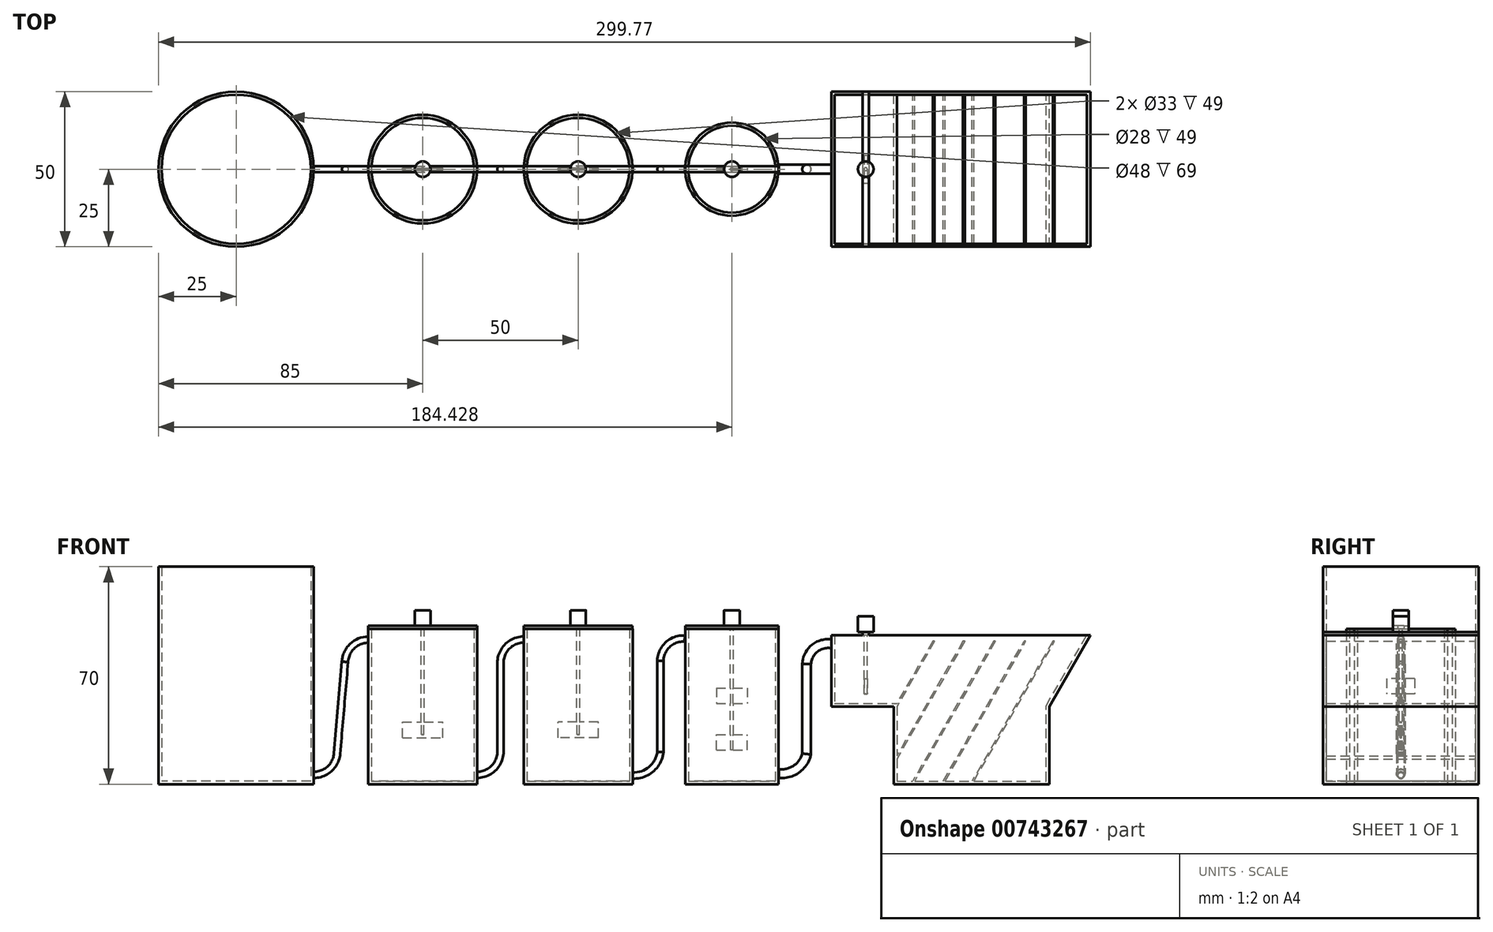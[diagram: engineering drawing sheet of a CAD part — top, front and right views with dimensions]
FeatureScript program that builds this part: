
annotation { "Feature Type Name" : "Feature", "Feature Type Description" : "" }
export const myFeature = defineFeature(function(context is Context, id is Id, definition is map)
    precondition{}
    {
        {
            var Q0;
            Q0=qCreatedBy(makeId("Top.planeOp"),FACE);
            var sketch = newSketch(context, id + "F0", { "sketchPlane" : qUnion([Q0])});
            skCircle(sketch, "E0", {"center": v(0, 0) * mm, "radius": 25 * mm});
            skCircle(sketch, "E1", {"center": v(159.43, 0) * mm, "radius": 15 * mm});
            skSolve(sketch);
        }
        {
            var Q0;
            Q0=makeQuery(id+"F0.imprint","IMPRINT",FACE,{"disambiguationData":[TD([[makeQuery(id+"F0.imprint","IMPRINT",EDGE,{"derivedFrom":sQuery(id+"F0.wireOp",EDGE,"E0")}),1.0]])]});
            extrude(context, id + "F1", {"entities" : qUnion([Q0]), "depth" : 70 * mm, "offsetDistance" : 25 * mm});
        }
        {
            var Q0;
            Q0=makeQuery(id+"F1.opExtrude","CAP_FACE",FACE,{"disambiguationData":[OSD([sQuery(id+"F0.wireOp",EDGE,"E0")])],"isStart":false});
            shell(context, id + "F2", {"entities" : qUnion([Q0]), "thickness" : 1 * mm});
        }
        {
            var Q0;
            Q0=qCreatedBy(makeId("Top.planeOp"),FACE);
            var sketch = newSketch(context, id + "F3", { "sketchPlane" : qUnion([Q0])});
            skCircle(sketch, "E2", {"center": v(60, 0) * mm, "radius": 17.5 * mm});
            skSolve(sketch);
        }
        {
            var Q0;
            Q0=makeQuery(id+"F3.imprint","IMPRINT",FACE,{"disambiguationData":[TD([[makeQuery(id+"F3.imprint","IMPRINT",EDGE,{"derivedFrom":sQuery(id+"F3.wireOp",EDGE,"E2")}),1.0]])]});
            extrude(context, id + "F4", {"entities" : qUnion([Q0]), "depth" : 50 * mm, "offsetDistance" : 25 * mm});
        }
        {
            var Q0;
            Q0=makeQuery(id+"F4.opExtrude","CAP_FACE",FACE,{"disambiguationData":[OSD([sQuery(id+"F3.wireOp",EDGE,"E2")])],"isStart":false});
            var Q1;
            Q1=makeQuery(id+"F4.opExtrude","CAP_FACE",FACE,{"disambiguationData":[OSD([sQuery(id+"F3.wireOp",EDGE,"7fbXtZi6-3e4z-6Rhc-ttlS-KZZd6jYo581z")])],"isStart":false});
            shell(context, id + "F5", {"entities" : qUnion([Q0, Q1]), "thickness" : 1 * mm});
        }
        {
            var Q0;
            Q0=makeQuery(id+"F4.opExtrude","CAP_FACE",FACE,{"disambiguationData":[OSD([sQuery(id+"F3.wireOp",EDGE,"E2")])],"isStart":false});
            var sketch = newSketch(context, id + "F6", { "sketchPlane" : qUnion([Q0])});
            skLineSegment(sketch, "E3.bottom", {"start": v(42.53, 1) * mm, "end": v(77.47, 1) * mm});
            skLineSegment(sketch, "E3.top", {"start": v(42.53, -1) * mm, "end": v(77.47, -1) * mm});
            skLineSegment(sketch, "E3.left", {"start": v(42.53, 1) * mm, "end": v(42.53, -1) * mm});
            skLineSegment(sketch, "E3.right", {"start": v(77.47, 1) * mm, "end": v(77.47, -1) * mm});
            skSolve(sketch);
        }
        {
            var Q0;
            {var subQ0=sQuery(id+"F6.wireOp",EDGE,"E3.left");Q0=makeQuery(id+"F6.imprint","IMPRINT",FACE,{"disambiguationData":[TD([[makeQuery(id+"F6.imprint","IMPRINT",EDGE,{"derivedFrom":subQ0}),1.0]])]});}
            var Q1;
            {var subQ0=sQuery(id+"F6.wireOp",EDGE,"E3.right");Q1=makeQuery(id+"F6.imprint","IMPRINT",FACE,{"disambiguationData":[TD([[makeQuery(id+"F6.imprint","IMPRINT",EDGE,{"derivedFrom":subQ0}),-1.0]])]});}
            var Q2;
            {var subQ0=sQuery(id+"F6.wireOp",EDGE,"E3.bottom");var subQ1=sQuery(id+"F3.wireOp",EDGE,"E2");var subQ2=makeQuery(id+"F5.opShell","OFFSET_EDGE",EDGE,{"disambiguationData":[OSD([subQ1]),TDD([makeQuery(id+"F4.opExtrude","CAP_EDGE",EDGE,{"disambiguationData":[OSD([subQ1])],"isStart":false})])]});var subQ3=makeQuery(id+"F6.imprint","INTERSECT",VERTEX,{"disambiguationData":[OD(0.0)],"derivedFrom":[subQ2,subQ0]});Q2=makeQuery(id+"F6.imprint","IMPRINT",FACE,{"disambiguationData":[TD([[makeQuery(id+"F6.imprint","IMPRINT",EDGE,{"disambiguationData":[TD([[subQ3,-1.0]])],"derivedFrom":subQ0}),-1.0]])]});}
            extrude(context, id + "F7", {"entities" : qUnion([Q0, Q1, Q2]), "operationType" : NewBodyOperationType.ADD, "depth" : 1 * mm, "offsetDistance" : 25 * mm});
        }
        {
            var Q0;
            Q0=makeQuery(id+"F7.opExtrude","CAP_FACE",FACE,{"disambiguationData":[OSD([sQuery(id+"F6.wireOp",EDGE,"E3.bottom"),sQuery(id+"F6.wireOp",EDGE,"E3.top"),sQuery(id+"F6.wireOp",EDGE,"E3.left"),sQuery(id+"F6.wireOp",EDGE,"E3.right")])],"isStart":false});
            var sketch = newSketch(context, id + "F8", { "sketchPlane" : qUnion([Q0])});
            skCircle(sketch, "E4.0.0", {"center": v(60, 0) * mm, "radius": 16.5 * mm});
            skCircle(sketch, "E5", {"center": v(60, 0) * mm, "radius": 2.5 * mm});
            skSolve(sketch);
        }
        {
            var Q0;
            {var subQ0=sQuery(id+"F8.wireOp",EDGE,"E5");var subQ1=makeQuery(id+"F7.opExtrude","CAP_EDGE",EDGE,{"disambiguationData":[OSD([sQuery(id+"F6.wireOp",EDGE,"E3.bottom")])],"isStart":false});var subQ2=makeQuery(id+"F8.imprint","INTERSECT",VERTEX,{"disambiguationData":[OD(0.0)],"derivedFrom":[subQ1,subQ0]});Q0=makeQuery(id+"F8.imprint","IMPRINT",FACE,{"disambiguationData":[TD([[makeQuery(id+"F8.imprint","IMPRINT",EDGE,{"disambiguationData":[TD([[subQ2,-1.0]])],"derivedFrom":subQ0}),1.0]])]});}
            var Q1;
            {var subQ0=sQuery(id+"F8.wireOp",EDGE,"E5");var subQ1=makeQuery(id+"F7.opExtrude","CAP_EDGE",EDGE,{"disambiguationData":[OSD([sQuery(id+"F6.wireOp",EDGE,"E3.top")])],"isStart":false});var subQ2=makeQuery(id+"F8.imprint","INTERSECT",VERTEX,{"disambiguationData":[OD(0.0)],"derivedFrom":[subQ1,subQ0]});Q1=makeQuery(id+"F8.imprint","IMPRINT",FACE,{"disambiguationData":[TD([[makeQuery(id+"F8.imprint","IMPRINT",EDGE,{"disambiguationData":[TD([[subQ2,-1.0]])],"derivedFrom":subQ0}),1.0]])]});}
            var Q2;
            {var subQ0=sQuery(id+"F8.wireOp",EDGE,"E5");var subQ1=makeQuery(id+"F7.opExtrude","CAP_EDGE",EDGE,{"disambiguationData":[OSD([sQuery(id+"F6.wireOp",EDGE,"E3.bottom")])],"isStart":false});var subQ2=makeQuery(id+"F8.imprint","INTERSECT",VERTEX,{"disambiguationData":[OD(0.0)],"derivedFrom":[subQ1,subQ0]});Q2=makeQuery(id+"F8.imprint","IMPRINT",FACE,{"disambiguationData":[TD([[makeQuery(id+"F8.imprint","IMPRINT",EDGE,{"disambiguationData":[TD([[subQ2,1.0]])],"derivedFrom":subQ0}),1.0]])]});}
            extrude(context, id + "F9", {"entities" : qUnion([Q0, Q1, Q2]), "operationType" : NewBodyOperationType.ADD, "depth" : 5 * mm, "offsetDistance" : 25 * mm});
        }
        {
            var Q0;
            Q0=makeQuery(id+"F9.opExtrude","CAP_FACE",FACE,{"disambiguationData":[OSD([sQuery(id+"F8.wireOp",EDGE,"E5")])],"isStart":false});
            var sketch = newSketch(context, id + "F10", { "sketchPlane" : qUnion([Q0])});
            skCircle(sketch, "E6", {"center": v(60, 0) * mm, "radius": 0.5 * mm});
            skSolve(sketch);
        }
        {
            var Q0;
            Q0=makeQuery(id+"F10.imprint","IMPRINT",FACE,{"disambiguationData":[TD([[makeQuery(id+"F10.imprint","IMPRINT",EDGE,{"derivedFrom":sQuery(id+"F10.wireOp",EDGE,"E6")}),1.0]])]});
            extrude(context, id + "F11", {"entities" : qUnion([Q0]), "operationType" : NewBodyOperationType.ADD, "oppositeDirection" : true, "depth" : 40 * mm, "offsetDistance" : 25 * mm});
        }
        {
            var Q0;
            Q0=qCreatedBy(makeId("Right.planeOp"),FACE);
            cPlane(context, id + "F12", {"entities" : qUnion([Q0]), "cplaneType" : CPlaneType.OFFSET, "offset" : 85 * mm, "width" : 150 * mm, "height" : 150 * mm});
        }
        {
            var Q0;
            Q0=makeQuery(id+"F4.opExtrude","CAP_FACE",FACE,{"disambiguationData":[OSD([sQuery(id+"F3.wireOp",EDGE,"E2")])],"isStart":true});
            cPlane(context, id + "F13", {"entities" : qUnion([Q0]), "cplaneType" : CPlaneType.OFFSET, "offset" : 20 * mm, "oppositeDirection" : true, "width" : 150 * mm, "height" : 150 * mm});
        }
        {
            var Q0;
            Q0=qCreatedBy(id+"F13.planeOp",FACE);
            var sketch = newSketch(context, id + "F14", { "sketchPlane" : qUnion([Q0])});
            skLineSegment(sketch, "E7.bottom", {"start": v(53.5, 0.3) * mm, "end": v(66.5, 0.3) * mm});
            skLineSegment(sketch, "E7.top", {"start": v(53.5, -0.3) * mm, "end": v(66.5, -0.3) * mm});
            skLineSegment(sketch, "E7.left", {"start": v(53.5, 0.3) * mm, "end": v(53.5, -0.3) * mm});
            skLineSegment(sketch, "E7.right", {"start": v(66.5, 0.3) * mm, "end": v(66.5, -0.3) * mm});
            skSolve(sketch);
        }
        {
            var Q0;
            Q0=makeQuery(id+"F14.imprint","IMPRINT",FACE,{"disambiguationData":[TD([[makeQuery(id+"F14.imprint","IMPRINT",EDGE,{"derivedFrom":sQuery(id+"F14.wireOp",EDGE,"E7.bottom")}),-1.0]])]});
            extrude(context, id + "F15", {"entities" : qUnion([Q0]), "operationType" : NewBodyOperationType.ADD, "depth" : 5 * mm, "offsetDistance" : 25 * mm});
        }
        {
            var Q0;
            Q0=makeQuery(id+"F4.opExtrude","SWEPT_BODY",BODY,{"disambiguationData":[OSD([sQuery(id+"F3.wireOp",EDGE,"E2")])]});
            var Q1;
            Q1=qCreatedBy(id+"F12.planeOp",FACE);
            mirror(context, id + "F16", {"entities" : qUnion([Q0]), "mirrorPlane" : qUnion([Q1])});
        }
        {
            var Q0;
            Q0=makeQuery(id+"F0.imprint","IMPRINT",FACE,{"disambiguationData":[TD([[makeQuery(id+"F0.imprint","IMPRINT",EDGE,{"derivedFrom":sQuery(id+"F0.wireOp",EDGE,"E1")}),1.0]])]});
            extrude(context, id + "F17", {"entities" : qUnion([Q0]), "depth" : 50 * mm, "offsetDistance" : 25 * mm});
        }
        {
            var Q0;
            Q0=makeQuery(id+"F17.opExtrude","CAP_FACE",FACE,{"disambiguationData":[OSD([sQuery(id+"F0.wireOp",EDGE,"E1")])],"isStart":false});
            shell(context, id + "F18", {"entities" : qUnion([Q0]), "thickness" : 1 * mm});
        }
        {
            var Q0;
            Q0=makeQuery(id+"F17.opExtrude","CAP_FACE",FACE,{"disambiguationData":[OSD([sQuery(id+"F0.wireOp",EDGE,"E1")])],"isStart":false});
            var sketch = newSketch(context, id + "F19", { "sketchPlane" : qUnion([Q0])});
            skLineSegment(sketch, "E8.bottom", {"start": v(144.46, 1) * mm, "end": v(174.4, 1) * mm});
            skLineSegment(sketch, "E8.top", {"start": v(144.46, -1) * mm, "end": v(174.4, -1) * mm});
            skLineSegment(sketch, "E8.left", {"start": v(144.46, 1) * mm, "end": v(144.46, -1) * mm});
            skLineSegment(sketch, "E8.right", {"start": v(174.4, 1) * mm, "end": v(174.4, -1) * mm});
            skSolve(sketch);
        }
        {
            var Q0;
            {var subQ0=sQuery(id+"F19.wireOp",EDGE,"E8.bottom");var subQ1=sQuery(id+"F0.wireOp",EDGE,"E1");var subQ2=makeQuery(id+"F18.opShell","OFFSET_EDGE",EDGE,{"disambiguationData":[OSD([subQ1]),TDD([makeQuery(id+"F17.opExtrude","CAP_EDGE",EDGE,{"disambiguationData":[OSD([subQ1])],"isStart":false})])]});var subQ3=makeQuery(id+"F19.imprint","INTERSECT",VERTEX,{"disambiguationData":[OD(0.0)],"derivedFrom":[subQ2,subQ0]});Q0=makeQuery(id+"F19.imprint","IMPRINT",FACE,{"disambiguationData":[TD([[makeQuery(id+"F19.imprint","IMPRINT",EDGE,{"disambiguationData":[TD([[subQ3,-1.0]])],"derivedFrom":subQ0}),-1.0]])]});}
            var Q1;
            {var subQ0=sQuery(id+"F19.wireOp",EDGE,"E8.left");Q1=makeQuery(id+"F19.imprint","IMPRINT",FACE,{"disambiguationData":[TD([[makeQuery(id+"F19.imprint","IMPRINT",EDGE,{"derivedFrom":subQ0}),1.0]])]});}
            var Q2;
            {var subQ0=sQuery(id+"F19.wireOp",EDGE,"E8.right");Q2=makeQuery(id+"F19.imprint","IMPRINT",FACE,{"disambiguationData":[TD([[makeQuery(id+"F19.imprint","IMPRINT",EDGE,{"derivedFrom":subQ0}),-1.0]])]});}
            extrude(context, id + "F20", {"entities" : qUnion([Q0, Q1, Q2]), "operationType" : NewBodyOperationType.ADD, "depth" : 1 * mm, "offsetDistance" : 25 * mm});
        }
        {
            var Q0;
            Q0=makeQuery(id+"F20.opExtrude","CAP_FACE",FACE,{"disambiguationData":[OSD([sQuery(id+"F19.wireOp",EDGE,"E8.bottom"),sQuery(id+"F19.wireOp",EDGE,"E8.top"),sQuery(id+"F19.wireOp",EDGE,"E8.left"),sQuery(id+"F19.wireOp",EDGE,"E8.right")])],"isStart":false});
            var sketch = newSketch(context, id + "F21", { "sketchPlane" : qUnion([Q0])});
            skArc(sketch, "E9.0", {"start": v(173.4, 1) * mm, "mid": v(159.43, 14) * mm, "end": v(145.46, 1) * mm});
            skCircle(sketch, "E10", {"center": v(159.43, 0) * mm, "radius": 0.5 * mm});
            skSolve(sketch);
        }
        {
            var Q0;
            Q0=makeQuery(id+"F21.imprint","IMPRINT",FACE,{"disambiguationData":[TD([[makeQuery(id+"F21.imprint","IMPRINT",EDGE,{"derivedFrom":sQuery(id+"F21.wireOp",EDGE,"E10")}),1.0]])]});
            extrude(context, id + "F22", {"entities" : qUnion([Q0]), "operationType" : NewBodyOperationType.ADD, "oppositeDirection" : true, "depth" : 40 * mm, "offsetDistance" : 25 * mm});
        }
        {
            var Q0;
            Q0=makeQuery(id+"F20.opExtrude","CAP_FACE",FACE,{"disambiguationData":[OSD([sQuery(id+"F19.wireOp",EDGE,"E8.bottom"),sQuery(id+"F19.wireOp",EDGE,"E8.top"),sQuery(id+"F19.wireOp",EDGE,"E8.left"),sQuery(id+"F19.wireOp",EDGE,"E8.right")])],"isStart":false});
            cPlane(context, id + "F23", {"entities" : qUnion([Q0]), "cplaneType" : CPlaneType.OFFSET, "offset" : 35 * mm, "oppositeDirection" : true, "width" : 150 * mm, "height" : 150 * mm});
        }
        {
            var Q0;
            Q0=qCreatedBy(id+"F23.planeOp",FACE);
            var sketch = newSketch(context, id + "F24", { "sketchPlane" : qUnion([Q0])});
            skLineSegment(sketch, "E11.bottom", {"start": v(154.43, 0.3) * mm, "end": v(164.43, 0.3) * mm});
            skLineSegment(sketch, "E11.top", {"start": v(154.43, -0.3) * mm, "end": v(164.43, -0.3) * mm});
            skLineSegment(sketch, "E11.left", {"start": v(154.43, 0.3) * mm, "end": v(154.43, -0.3) * mm});
            skLineSegment(sketch, "E11.right", {"start": v(164.43, 0.3) * mm, "end": v(164.43, -0.3) * mm});
            skSolve(sketch);
        }
        {
            var Q0;
            Q0=makeQuery(id+"F24.imprint","IMPRINT",FACE,{"disambiguationData":[TD([[makeQuery(id+"F24.imprint","IMPRINT",EDGE,{"derivedFrom":sQuery(id+"F24.wireOp",EDGE,"E11.bottom")}),-1.0]])]});
            extrude(context, id + "F25", {"entities" : qUnion([Q0]), "operationType" : NewBodyOperationType.ADD, "oppositeDirection" : true, "depth" : 5 * mm, "offsetDistance" : 25 * mm});
        }
        {
            var Q0;
            Q0=makeQuery(id+"F20.opExtrude","CAP_FACE",FACE,{"disambiguationData":[OSD([sQuery(id+"F19.wireOp",EDGE,"E8.bottom"),sQuery(id+"F19.wireOp",EDGE,"E8.top"),sQuery(id+"F19.wireOp",EDGE,"E8.left"),sQuery(id+"F19.wireOp",EDGE,"E8.right")])],"isStart":false});
            cPlane(context, id + "F26", {"entities" : qUnion([Q0]), "cplaneType" : CPlaneType.OFFSET, "offset" : 25 * mm, "oppositeDirection" : true, "width" : 150 * mm, "height" : 150 * mm});
        }
        {
            var Q0;
            Q0=qCreatedBy(id+"F26.planeOp",FACE);
            var sketch = newSketch(context, id + "F27", { "sketchPlane" : qUnion([Q0])});
            skLineSegment(sketch, "E12.0", {"start": v(154.43, 0.3) * mm, "end": v(159.03, 0.3) * mm});
            skPoint(sketch, "E13.0", {"position": v(154.43, 0) * mm});
            skLineSegment(sketch, "E14.0", {"start": v(154.43, 0.3) * mm, "end": v(154.43, -0.3) * mm});
            skLineSegment(sketch, "E15.0", {"start": v(154.43, -0.3) * mm, "end": v(159.03, -0.3) * mm});
            skLineSegment(sketch, "E16.0", {"start": v(159.83, 0.3) * mm, "end": v(164.43, 0.3) * mm});
            skLineSegment(sketch, "E17.0", {"start": v(164.43, 0.3) * mm, "end": v(164.43, -0.3) * mm});
            skLineSegment(sketch, "E18.0", {"start": v(159.83, -0.3) * mm, "end": v(164.43, -0.3) * mm});
            skLineSegment(sketch, "E19", {"start": v(159.03, 0.3) * mm, "end": v(159.83, 0.3) * mm});
            skLineSegment(sketch, "E20", {"start": v(159.83, -0.3) * mm, "end": v(159.03, -0.3) * mm});
            skSolve(sketch);
        }
        {
            var Q0;
            Q0=makeQuery(id+"F27.imprint","IMPRINT",FACE,{"disambiguationData":[TD([[makeQuery(id+"F27.imprint","IMPRINT",EDGE,{"derivedFrom":sQuery(id+"F27.wireOp",EDGE,"E12.0")}),-1.0]])]});
            extrude(context, id + "F28", {"entities" : qUnion([Q0]), "operationType" : NewBodyOperationType.ADD, "depth" : 5 * mm, "offsetDistance" : 25 * mm});
        }
        {
            var Q0;
            Q0=makeQuery(id+"F20.opExtrude","CAP_FACE",FACE,{"disambiguationData":[OSD([sQuery(id+"F19.wireOp",EDGE,"E8.bottom"),sQuery(id+"F19.wireOp",EDGE,"E8.top"),sQuery(id+"F19.wireOp",EDGE,"E8.left"),sQuery(id+"F19.wireOp",EDGE,"E8.right")])],"isStart":false});
            var sketch = newSketch(context, id + "F29", { "sketchPlane" : qUnion([Q0])});
            skCircle(sketch, "E21", {"center": v(159.43, 0) * mm, "radius": 2.5 * mm});
            skPoint(sketch, "E21.centerSnap0", {"position": v(159.43, -1) * mm});
            skSolve(sketch);
        }
        {
            var Q0;
            {var subQ0=sQuery(id+"F29.wireOp",EDGE,"E21");var subQ1=makeQuery(id+"F20.opExtrude","CAP_EDGE",EDGE,{"disambiguationData":[OSD([sQuery(id+"F19.wireOp",EDGE,"E8.bottom")])],"isStart":false});var subQ2=makeQuery(id+"F29.imprint","INTERSECT",VERTEX,{"disambiguationData":[OD(0.0)],"derivedFrom":[subQ1,subQ0]});Q0=makeQuery(id+"F29.imprint","IMPRINT",FACE,{"disambiguationData":[TD([[makeQuery(id+"F29.imprint","IMPRINT",EDGE,{"disambiguationData":[TD([[subQ2,1.0]])],"derivedFrom":subQ0}),1.0]])]});}
            var Q1;
            {var subQ0=sQuery(id+"F29.wireOp",EDGE,"E21");var subQ1=makeQuery(id+"F20.opExtrude","CAP_EDGE",EDGE,{"disambiguationData":[OSD([sQuery(id+"F19.wireOp",EDGE,"E8.top")])],"isStart":false});var subQ2=makeQuery(id+"F29.imprint","INTERSECT",VERTEX,{"disambiguationData":[OD(0.0)],"derivedFrom":[subQ1,subQ0]});Q1=makeQuery(id+"F29.imprint","IMPRINT",FACE,{"disambiguationData":[TD([[makeQuery(id+"F29.imprint","IMPRINT",EDGE,{"disambiguationData":[TD([[subQ2,-1.0]])],"derivedFrom":subQ0}),1.0]])]});}
            var Q2;
            {var subQ0=sQuery(id+"F29.wireOp",EDGE,"E21");var subQ1=makeQuery(id+"F20.opExtrude","CAP_EDGE",EDGE,{"disambiguationData":[OSD([sQuery(id+"F19.wireOp",EDGE,"E8.bottom")])],"isStart":false});var subQ2=makeQuery(id+"F29.imprint","INTERSECT",VERTEX,{"disambiguationData":[OD(0.0)],"derivedFrom":[subQ1,subQ0]});Q2=makeQuery(id+"F29.imprint","IMPRINT",FACE,{"disambiguationData":[TD([[makeQuery(id+"F29.imprint","IMPRINT",EDGE,{"disambiguationData":[TD([[subQ2,-1.0]])],"derivedFrom":subQ0}),1.0]])]});}
            extrude(context, id + "F30", {"entities" : qUnion([Q0, Q1, Q2]), "operationType" : NewBodyOperationType.ADD, "depth" : 5 * mm, "offsetDistance" : 25 * mm});
        }
        {
            var Q0;
            Q0=qCreatedBy(makeId("Front.planeOp"),FACE);
            var sketch = newSketch(context, id + "F31", { "sketchPlane" : qUnion([Q0])});
            skLineSegment(sketch, "E22", {"start": v(191.49, 48) * mm, "end": v(191.49, 25) * mm});
            skLineSegment(sketch, "E23", {"start": v(191.49, 25) * mm, "end": v(211.49, 25) * mm});
            skLineSegment(sketch, "E24", {"start": v(211.49, 25) * mm, "end": v(211.49, 0) * mm});
            skLineSegment(sketch, "E25", {"start": v(211.49, 0) * mm, "end": v(261.49, 0) * mm});
            skLineSegment(sketch, "E26", {"start": v(261.49, 0) * mm, "end": v(261.49, 25) * mm});
            skLineSegment(sketch, "E27", {"start": v(261.49, 25) * mm, "end": v(274.77, 48) * mm});
            skLineSegment(sketch, "E28", {"start": v(274.77, 48) * mm, "end": v(191.49, 48) * mm});
            skSolve(sketch);
        }
        {
            var Q0;
            Q0=makeQuery(id+"F31.imprint","IMPRINT",FACE,{"disambiguationData":[TD([[makeQuery(id+"F31.imprint","IMPRINT",EDGE,{"derivedFrom":sQuery(id+"F31.wireOp",EDGE,"E22")}),1.0]])]});
            extrude(context, id + "F32", {"entities" : qUnion([Q0]), "endBound" : BoundingType.SYMMETRIC, "depth" : 50 * mm, "offsetDistance" : 25 * mm});
        }
        {
            var Q0;
            Q0=makeQuery(id+"F32.opExtrude","SWEPT_FACE",FACE,{"disambiguationData":[OSD([sQuery(id+"F31.wireOp",EDGE,"E28")])]});
            shell(context, id + "F33", {"entities" : qUnion([Q0]), "thickness" : 1 * mm});
        }
        {
            var Q0;
            Q0=qCreatedBy(makeId("Front.planeOp"),FACE);
            var sketch = newSketch(context, id + "F34", { "sketchPlane" : qUnion([Q0])});
            skLineSegment(sketch, "E29.0", {"start": v(264.37, 48) * mm, "end": v(263.8, 48) * mm});
            skLineSegment(sketch, "E30.0", {"start": v(212.49, 26) * mm, "end": v(212.49, 25) * mm});
            skLineSegment(sketch, "E31.0", {"start": v(227.42, 1) * mm, "end": v(228, 1) * mm});
            skLineSegment(sketch, "E32", {"start": v(212.49, 26) * mm, "end": v(224.03, 46) * mm});
            skLineSegment(sketch, "E33", {"start": v(212.49, 25) * mm, "end": v(224.61, 46) * mm});
            skLineSegment(sketch, "E34", {"start": v(263.22, 46) * mm, "end": v(237.24, 1) * mm});
            skLineSegment(sketch, "E35", {"start": v(253.98, 46) * mm, "end": v(228, 1) * mm});
            skLineSegment(sketch, "E36", {"start": v(253.4, 46) * mm, "end": v(227.42, 1) * mm});
            skLineSegment(sketch, "E37", {"start": v(236.66, 1) * mm, "end": v(262.64, 46) * mm});
            skPoint(sketch, "E38.0.2.start.orphan", {"position": v(191.49, 48) * mm});
            skPoint(sketch, "E38.0.3.start.orphan", {"position": v(191.49, 25) * mm});
            skPoint(sketch, "E38.0.4.start.orphan", {"position": v(211.49, 25) * mm});
            skLineSegment(sketch, "E39.trimOffspring", {"start": v(236.66, 1) * mm, "end": v(237.24, 1) * mm});
            skPoint(sketch, "E38.0.5.start.orphan", {"position": v(211.49, 0) * mm});
            skPoint(sketch, "E40.orphan", {"position": v(212.49, 1) * mm});
            skPoint(sketch, "E41.orphan", {"position": v(260.49, 1) * mm});
            skPoint(sketch, "E38.0.6.start.orphan", {"position": v(261.49, 0) * mm});
            skLineSegment(sketch, "E42.trimOffspring", {"start": v(225.77, 48) * mm, "end": v(225.19, 48) * mm});
            skLineSegment(sketch, "E43.trimOffspring", {"start": v(255.14, 48) * mm, "end": v(254.56, 48) * mm});
            skPoint(sketch, "E38.0.0.end.orphan", {"position": v(274.77, 48) * mm});
            skPoint(sketch, "E38.0.0.start.orphan", {"position": v(261.49, 25) * mm});
            skLineSegment(sketch, "E44.0.0", {"start": v(261.49, 25) * mm, "end": v(274.77, 48) * mm});
            skLineSegment(sketch, "E44.0.1", {"start": v(274.77, 48) * mm, "end": v(191.49, 48) * mm});
            skLineSegment(sketch, "E44.0.2", {"start": v(191.49, 48) * mm, "end": v(191.49, 25) * mm});
            skLineSegment(sketch, "E44.0.3", {"start": v(191.49, 25) * mm, "end": v(211.49, 25) * mm});
            skLineSegment(sketch, "E44.0.4", {"start": v(211.49, 25) * mm, "end": v(211.49, 0) * mm});
            skLineSegment(sketch, "E44.0.5", {"start": v(211.49, 0) * mm, "end": v(261.49, 0) * mm});
            skLineSegment(sketch, "E44.0.6", {"start": v(261.49, 0) * mm, "end": v(261.49, 25) * mm});
            skLineSegment(sketch, "E45.0", {"start": v(212.49, 1) * mm, "end": v(260.49, 1) * mm});
            skLineSegment(sketch, "E46.0", {"start": v(212.49, 26) * mm, "end": v(212.49, 1) * mm});
            skLineSegment(sketch, "E47", {"start": v(218.19, 1) * mm, "end": v(244.17, 46) * mm});
            skLineSegment(sketch, "E48", {"start": v(217.6, 1) * mm, "end": v(243.59, 46) * mm});
            skLineSegment(sketch, "E49", {"start": v(212.49, 8.13) * mm, "end": v(234.35, 46) * mm});
            skLineSegment(sketch, "E50", {"start": v(212.49, 9.13) * mm, "end": v(233.77, 46) * mm});
            skLineSegment(sketch, "E51", {"start": v(224.03, 46) * mm, "end": v(224.61, 46) * mm});
            skLineSegment(sketch, "E52.trimOffspring", {"start": v(262.64, 46) * mm, "end": v(263.22, 46) * mm});
            skLineSegment(sketch, "E53.trimOffspring", {"start": v(253.4, 46) * mm, "end": v(253.98, 46) * mm});
            skLineSegment(sketch, "E54.trimOffspring", {"start": v(243.59, 46) * mm, "end": v(244.17, 46) * mm});
            skLineSegment(sketch, "E55.trimOffspring", {"start": v(233.77, 46) * mm, "end": v(234.35, 46) * mm});
            skSolve(sketch);
        }
        {
            var Q0;
            {var subQ0=sQuery(id+"F34.wireOp",EDGE,"E32");Q0=makeQuery(id+"F34.imprint","IMPRINT",FACE,{"disambiguationData":[TD([[makeQuery(id+"F34.imprint","IMPRINT",EDGE,{"derivedFrom":subQ0}),-1.0]])]});}
            var Q1;
            {var subQ0=sQuery(id+"F34.wireOp",EDGE,"E49");Q1=makeQuery(id+"F34.imprint","IMPRINT",FACE,{"disambiguationData":[TD([[makeQuery(id+"F34.imprint","IMPRINT",EDGE,{"derivedFrom":subQ0}),1.0]])]});}
            var Q2;
            {var subQ0=sQuery(id+"F34.wireOp",EDGE,"E47");Q2=makeQuery(id+"F34.imprint","IMPRINT",FACE,{"disambiguationData":[TD([[makeQuery(id+"F34.imprint","IMPRINT",EDGE,{"derivedFrom":subQ0}),1.0]])]});}
            var Q3;
            {var subQ0=sQuery(id+"F34.wireOp",EDGE,"E35");Q3=makeQuery(id+"F34.imprint","IMPRINT",FACE,{"disambiguationData":[TD([[makeQuery(id+"F34.imprint","IMPRINT",EDGE,{"derivedFrom":subQ0}),-1.0]])]});}
            var Q4;
            {var subQ0=sQuery(id+"F34.wireOp",EDGE,"E34");Q4=makeQuery(id+"F34.imprint","IMPRINT",FACE,{"disambiguationData":[TD([[makeQuery(id+"F34.imprint","IMPRINT",EDGE,{"derivedFrom":subQ0}),-1.0]])]});}
            extrude(context, id + "F35", {"entities" : qUnion([Q0, Q1, Q2, Q3, Q4]), "operationType" : NewBodyOperationType.ADD, "endBound" : BoundingType.SYMMETRIC, "depth" : 50 * mm, "offsetDistance" : 25 * mm});
        }
        {
            var Q0;
            Q0=makeQuery(id+"F32.opExtrude","SWEPT_FACE",FACE,{"disambiguationData":[OSD([sQuery(id+"F31.wireOp",EDGE,"E28")])]});
            var sketch = newSketch(context, id + "F36", { "sketchPlane" : qUnion([Q0])});
            skLineSegment(sketch, "E56.bottom", {"start": v(201.49, 25) * mm, "end": v(203.49, 25) * mm});
            skLineSegment(sketch, "E56.top", {"start": v(201.49, -25) * mm, "end": v(203.49, -25) * mm});
            skLineSegment(sketch, "E56.left", {"start": v(201.49, 25) * mm, "end": v(201.49, -25) * mm});
            skLineSegment(sketch, "E56.right", {"start": v(203.49, 25) * mm, "end": v(203.49, -25) * mm});
            skSolve(sketch);
        }
        {
            var Q0;
            {var subQ0=sQuery(id+"F36.wireOp",EDGE,"E56.left");var subQ1=sQuery(id+"F31.wireOp",EDGE,"E28");var subQ2=makeQuery(id+"F33.opShell","OFFSET_EDGE",EDGE,{"disambiguationData":[OSD([subQ1]),TDD([makeQuery(id+"F32.opExtrude","CAP_EDGE",EDGE,{"disambiguationData":[OSD([subQ1])],"isStart":true})])]});var subQ3=makeQuery(id+"F36.imprint","INTERSECT",VERTEX,{"derivedFrom":[subQ2,subQ0]});Q0=makeQuery(id+"F36.imprint","IMPRINT",FACE,{"disambiguationData":[TD([[makeQuery(id+"F36.imprint","IMPRINT",EDGE,{"disambiguationData":[TD([[subQ3,-1.0]])],"derivedFrom":subQ0}),1.0]])]});}
            var Q1;
            {var subQ0=sQuery(id+"F36.wireOp",EDGE,"E56.top");Q1=makeQuery(id+"F36.imprint","IMPRINT",FACE,{"disambiguationData":[TD([[makeQuery(id+"F36.imprint","IMPRINT",EDGE,{"derivedFrom":subQ0}),-1.0]])]});}
            var Q2;
            {var subQ0=sQuery(id+"F36.wireOp",EDGE,"E56.bottom");Q2=makeQuery(id+"F36.imprint","IMPRINT",FACE,{"disambiguationData":[TD([[makeQuery(id+"F36.imprint","IMPRINT",EDGE,{"derivedFrom":subQ0}),1.0]])]});}
            extrude(context, id + "F37", {"entities" : qUnion([Q0, Q1, Q2]), "operationType" : NewBodyOperationType.ADD, "depth" : 1 * mm, "offsetDistance" : 25 * mm});
        }
        {
            var Q0;
            Q0=makeQuery(id+"F37.opExtrude","CAP_FACE",FACE,{"disambiguationData":[OSD([sQuery(id+"F36.wireOp",EDGE,"E56.bottom"),sQuery(id+"F36.wireOp",EDGE,"E56.top"),sQuery(id+"F36.wireOp",EDGE,"E56.left"),sQuery(id+"F36.wireOp",EDGE,"E56.right")])],"isStart":false});
            var sketch = newSketch(context, id + "F38", { "sketchPlane" : qUnion([Q0])});
            skCircle(sketch, "E57", {"center": v(202.49, 0) * mm, "radius": 0.5 * mm});
            skSolve(sketch);
        }
        {
            var Q0;
            Q0=makeQuery(id+"F38.imprint","IMPRINT",FACE,{"disambiguationData":[TD([[makeQuery(id+"F38.imprint","IMPRINT",EDGE,{"derivedFrom":sQuery(id+"F38.wireOp",EDGE,"E57")}),1.0]])]});
            extrude(context, id + "F39", {"entities" : qUnion([Q0]), "operationType" : NewBodyOperationType.ADD, "oppositeDirection" : true, "depth" : 20 * mm, "offsetDistance" : 25 * mm});
        }
        {
            var Q0;
            Q0=makeQuery(id+"F37.opExtrude","CAP_FACE",FACE,{"disambiguationData":[OSD([sQuery(id+"F36.wireOp",EDGE,"E56.bottom"),sQuery(id+"F36.wireOp",EDGE,"E56.top"),sQuery(id+"F36.wireOp",EDGE,"E56.left"),sQuery(id+"F36.wireOp",EDGE,"E56.right")])],"isStart":false});
            cPlane(context, id + "F40", {"entities" : qUnion([Q0]), "cplaneType" : CPlaneType.OFFSET, "offset" : 20 * mm, "oppositeDirection" : true, "width" : 150 * mm, "height" : 150 * mm});
        }
        {
            var Q0;
            Q0=qCreatedBy(id+"F40.planeOp",FACE);
            var sketch = newSketch(context, id + "F41", { "sketchPlane" : qUnion([Q0])});
            skLineSegment(sketch, "E58.bottom", {"start": v(201.99, 4.5) * mm, "end": v(202.99, 4.5) * mm});
            skLineSegment(sketch, "E58.top", {"start": v(201.99, -4.5) * mm, "end": v(202.99, -4.5) * mm});
            skLineSegment(sketch, "E58.left", {"start": v(201.99, 4.5) * mm, "end": v(201.99, -4.5) * mm});
            skLineSegment(sketch, "E58.right", {"start": v(202.99, 4.5) * mm, "end": v(202.99, -4.5) * mm});
            skSolve(sketch);
        }
        {
            var Q0;
            Q0=makeQuery(id+"F41.imprint","IMPRINT",FACE,{"disambiguationData":[TD([[makeQuery(id+"F41.imprint","IMPRINT",EDGE,{"derivedFrom":sQuery(id+"F41.wireOp",EDGE,"E58.bottom")}),-1.0]])]});
            extrude(context, id + "F42", {"entities" : qUnion([Q0]), "depth" : 5 * mm, "offsetDistance" : 25 * mm});
        }
        {
            var Q0;
            Q0=makeQuery(id+"F37.opExtrude","CAP_FACE",FACE,{"disambiguationData":[OSD([sQuery(id+"F36.wireOp",EDGE,"E56.bottom"),sQuery(id+"F36.wireOp",EDGE,"E56.top"),sQuery(id+"F36.wireOp",EDGE,"E56.left"),sQuery(id+"F36.wireOp",EDGE,"E56.right")])],"isStart":false});
            var sketch = newSketch(context, id + "F43", { "sketchPlane" : qUnion([Q0])});
            skCircle(sketch, "E59.0", {"center": v(202.49, 0) * mm, "radius": 0.5 * mm});
            skCircle(sketch, "E60", {"center": v(202.49, 0) * mm, "radius": 2.5 * mm});
            skSolve(sketch);
        }
        {
            var Q0;
            Q0=makeQuery(id+"F43.imprint","IMPRINT",FACE,{"disambiguationData":[TD([[makeQuery(id+"F43.imprint","IMPRINT",EDGE,{"derivedFrom":sQuery(id+"F43.wireOp",EDGE,"E59.0")}),-1.0]])]});
            var Q1;
            {var subQ0=sQuery(id+"F43.wireOp",EDGE,"E60");var subQ1=makeQuery(id+"F37.opExtrude","CAP_EDGE",EDGE,{"disambiguationData":[OSD([sQuery(id+"F36.wireOp",EDGE,"E56.left")])],"isStart":false});var subQ2=makeQuery(id+"F43.imprint","INTERSECT",VERTEX,{"disambiguationData":[OD(0.0)],"derivedFrom":[subQ1,subQ0]});Q1=makeQuery(id+"F43.imprint","IMPRINT",FACE,{"disambiguationData":[TD([[makeQuery(id+"F43.imprint","IMPRINT",EDGE,{"disambiguationData":[TD([[subQ2,-1.0]])],"derivedFrom":subQ0}),1.0]])]});}
            var Q2;
            {var subQ0=sQuery(id+"F43.wireOp",EDGE,"E60");var subQ1=makeQuery(id+"F37.opExtrude","CAP_EDGE",EDGE,{"disambiguationData":[OSD([sQuery(id+"F36.wireOp",EDGE,"E56.right")])],"isStart":false});var subQ2=makeQuery(id+"F43.imprint","INTERSECT",VERTEX,{"disambiguationData":[OD(0.0)],"derivedFrom":[subQ1,subQ0]});Q2=makeQuery(id+"F43.imprint","IMPRINT",FACE,{"disambiguationData":[TD([[makeQuery(id+"F43.imprint","IMPRINT",EDGE,{"disambiguationData":[TD([[subQ2,1.0]])],"derivedFrom":subQ0}),1.0]])]});}
            var Q3;
            Q3=makeQuery(id+"F43.imprint","IMPRINT",FACE,{"disambiguationData":[TD([[makeQuery(id+"F43.imprint","IMPRINT",EDGE,{"derivedFrom":sQuery(id+"F43.wireOp",EDGE,"E59.0")}),1.0]])]});
            extrude(context, id + "F44", {"entities" : qUnion([Q0, Q1, Q2, Q3]), "operationType" : NewBodyOperationType.ADD, "depth" : 5 * mm, "offsetDistance" : 25 * mm});
        }
        {
            var Q0;
            Q0=qCreatedBy(makeId("Right.planeOp"),FACE);
            cPlane(context, id + "F45", {"entities" : qUnion([Q0]), "cplaneType" : CPlaneType.OFFSET, "offset" : 25 * mm, "width" : 150 * mm, "height" : 150 * mm});
        }
        {
            var Q0;
            Q0=qCreatedBy(id+"F45.planeOp",FACE);
            var sketch = newSketch(context, id + "F46", { "sketchPlane" : qUnion([Q0])});
            skCircle(sketch, "E61", {"center": v(0, 3) * mm, "radius": 1 * mm});
            skSolve(sketch);
        }
        {
            var Q0;
            Q0=qCreatedBy(makeId("Front.planeOp"),FACE);
            var sketch = newSketch(context, id + "F47", { "sketchPlane" : qUnion([Q0])});
            skLineSegment(sketch, "E62", {"start": v(25, 70) * mm, "end": v(25, 10.5) * mm});
            skArc(sketch, "E63", {"start": v(25, 3) * mm, "mid": v(30.07, 4.97) * mm, "end": v(32.47, 9.86) * mm});
            skLineSegment(sketch, "E64", {"start": v(42.5, 0) * mm, "end": v(42.5, 39) * mm});
            skArc(sketch, "E65", {"start": v(42.5, 46.5) * mm, "mid": v(37.33, 44.44) * mm, "end": v(35, 39.38) * mm});
            skLineSegment(sketch, "E66", {"start": v(35, 39.38) * mm, "end": v(32.47, 9.86) * mm});
            skSolve(sketch);
        }
        {
            var Q0;
            Q0=makeQuery(id+"F46.imprint","IMPRINT",FACE,{"disambiguationData":[TD([[makeQuery(id+"F46.imprint","IMPRINT",EDGE,{"derivedFrom":sQuery(id+"F46.wireOp",EDGE,"E61")}),1.0]])]});
            var Q1;
            Q1=sQuery(id+"F47.wireOp",EDGE,"E66");
            var Q2;
            Q2=sQuery(id+"F47.wireOp",EDGE,"E63");
            var Q3;
            Q3=sQuery(id+"F47.wireOp",EDGE,"E65");
            sweep(context, id + "F48", {"profiles" : qUnion([Q0]), "path" : qUnion([Q1, Q2, Q3])});
        }
        {
            var Q0;
            Q0=qCreatedBy(makeId("Right.planeOp"),FACE);
            cPlane(context, id + "F49", {"entities" : qUnion([Q0]), "cplaneType" : CPlaneType.OFFSET, "offset" : 77.5 * mm, "width" : 150 * mm, "height" : 150 * mm});
        }
        {
            var Q0;
            Q0=qCreatedBy(id+"F49.planeOp",FACE);
            var sketch = newSketch(context, id + "F50", { "sketchPlane" : qUnion([Q0])});
            skCircle(sketch, "E67", {"center": v(0, 3) * mm, "radius": 1 * mm});
            skSolve(sketch);
        }
        {
            var Q0;
            Q0=qCreatedBy(makeId("Front.planeOp"),FACE);
            var sketch = newSketch(context, id + "F51", { "sketchPlane" : qUnion([Q0])});
            skLineSegment(sketch, "E68", {"start": v(77.5, 50) * mm, "end": v(77.5, 0) * mm});
            skLineSegment(sketch, "E69", {"start": v(92.5, 0) * mm, "end": v(92.5, 50) * mm});
            skArc(sketch, "E70", {"start": v(77.5, 3) * mm, "mid": v(82.8, 5.2) * mm, "end": v(85, 10.5) * mm});
            skLineSegment(sketch, "E71", {"start": v(85, 39.01) * mm, "end": v(85, 10.5) * mm});
            skLineSegment(sketch, "E72.0", {"start": v(77.5, 4) * mm, "end": v(77.5, 2) * mm, "construction": true});
            skArc(sketch, "E73", {"start": v(92.5, 46.55) * mm, "mid": v(87.2, 44.33) * mm, "end": v(85, 39.01) * mm});
            skSolve(sketch);
        }
        {
            var Q0;
            Q0=makeQuery(id+"F50.imprint","IMPRINT",FACE,{"disambiguationData":[TD([[makeQuery(id+"F50.imprint","IMPRINT",EDGE,{"derivedFrom":sQuery(id+"F50.wireOp",EDGE,"E67")}),1.0]])]});
            var Q1;
            Q1=sQuery(id+"F51.wireOp",EDGE,"E70");
            var Q2;
            Q2=sQuery(id+"F51.wireOp",EDGE,"E71");
            var Q3;
            Q3=sQuery(id+"F51.wireOp",EDGE,"E73");
            sweep(context, id + "F52", {"profiles" : qUnion([Q0]), "path" : qUnion([Q1, Q2, Q3])});
        }
        {
            var Q0;
            Q0=qCreatedBy(makeId("Front.planeOp"),FACE);
            var sketch = newSketch(context, id + "F53", { "sketchPlane" : qUnion([Q0])});
            skLineSegment(sketch, "E74", {"start": v(136.43, 10.34) * mm, "end": v(136.43, 39.7) * mm});
            skArc(sketch, "E75", {"start": v(144.36, 46.88) * mm, "mid": v(138.86, 44.99) * mm, "end": v(136.43, 39.7) * mm});
            skArc(sketch, "E76", {"start": v(127.6, 2.79) * mm, "mid": v(133.5, 4.83) * mm, "end": v(136.43, 10.34) * mm});
            skSolve(sketch);
        }
        {
            var Q0;
            Q0=qCreatedBy(makeId("Right.planeOp"),FACE);
            cPlane(context, id + "F54", {"entities" : qUnion([Q0]), "cplaneType" : CPlaneType.OFFSET, "offset" : 127.5 * mm, "width" : 150 * mm, "height" : 150 * mm});
        }
        {
            var Q0;
            Q0=qCreatedBy(id+"F54.planeOp",FACE);
            var sketch = newSketch(context, id + "F55", { "sketchPlane" : qUnion([Q0])});
            skPoint(sketch, "E77.0", {"position": v(0, 2.79) * mm});
            skCircle(sketch, "E78", {"center": v(0, 2.79) * mm, "radius": 1 * mm});
            skSolve(sketch);
        }
        {
            var Q0;
            Q0=makeQuery(id+"F55.imprint","IMPRINT",FACE,{"disambiguationData":[TD([[makeQuery(id+"F55.imprint","IMPRINT",EDGE,{"derivedFrom":sQuery(id+"F55.wireOp",EDGE,"E78")}),1.0]])]});
            var Q1;
            Q1=sQuery(id+"F53.wireOp",EDGE,"E76");
            var Q2;
            Q2=sQuery(id+"F53.wireOp",EDGE,"E74");
            var Q3;
            Q3=sQuery(id+"F53.wireOp",EDGE,"E75");
            sweep(context, id + "F56", {"operationType" : NewBodyOperationType.ADD, "profiles" : qUnion([Q0]), "path" : qUnion([Q1, Q2, Q3])});
        }
        {
            var Q0;
            Q0=qCreatedBy(makeId("Front.planeOp"),FACE);
            var sketch = newSketch(context, id + "F57", { "sketchPlane" : qUnion([Q0])});
            skLineSegment(sketch, "E79", {"start": v(183.46, 38.72) * mm, "end": v(183.46, 9.71) * mm});
            skArc(sketch, "E80", {"start": v(174.49, 3.43) * mm, "mid": v(180.18, 4.86) * mm, "end": v(183.46, 9.71) * mm});
            skArc(sketch, "E81", {"start": v(191.54, 45.17) * mm, "mid": v(186.07, 43.74) * mm, "end": v(183.46, 38.72) * mm});
            skSolve(sketch);
        }
        {
            var Q0;
            Q0=qCreatedBy(makeId("Right.planeOp"),FACE);
            cPlane(context, id + "F58", {"entities" : qUnion([Q0]), "cplaneType" : CPlaneType.OFFSET, "offset" : 174.5 * mm, "width" : 150 * mm, "height" : 150 * mm});
        }
        {
            var Q0;
            Q0=qCreatedBy(id+"F58.planeOp",FACE);
            var sketch = newSketch(context, id + "F59", { "sketchPlane" : qUnion([Q0])});
            skPoint(sketch, "E82.0", {"position": v(0, 3.43) * mm});
            skCircle(sketch, "E83", {"center": v(0, 3.43) * mm, "radius": 1.43 * mm});
            skSolve(sketch);
        }
        {
            var Q0;
            Q0=makeQuery(id+"F59.imprint","IMPRINT",FACE,{"disambiguationData":[TD([[makeQuery(id+"F59.imprint","IMPRINT",EDGE,{"derivedFrom":sQuery(id+"F59.wireOp",EDGE,"E83")}),1.0]])]});
            var Q1;
            Q1=sQuery(id+"F57.wireOp",EDGE,"E80");
            var Q2;
            Q2=sQuery(id+"F57.wireOp",EDGE,"E79");
            var Q3;
            Q3=sQuery(id+"F57.wireOp",EDGE,"E81");
            sweep(context, id + "F60", {"operationType" : NewBodyOperationType.ADD, "profiles" : qUnion([Q0]), "path" : qUnion([Q1, Q2, Q3])});
        }
    });
